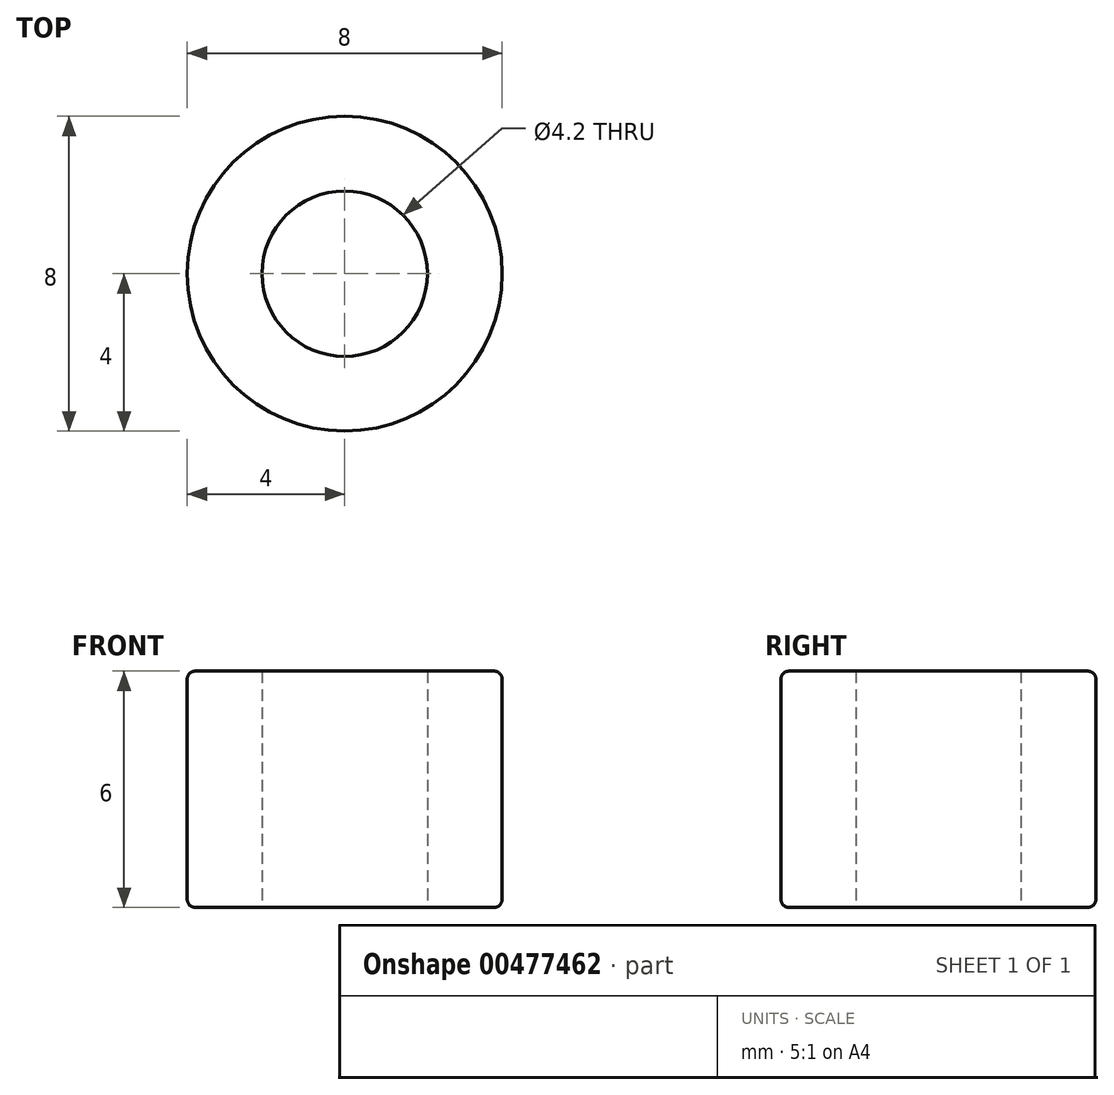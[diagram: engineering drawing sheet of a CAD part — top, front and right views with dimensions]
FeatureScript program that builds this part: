
annotation { "Feature Type Name" : "Feature", "Feature Type Description" : "" }
export const myFeature = defineFeature(function(context is Context, id is Id, definition is map)
    precondition{}
    {
        {
            var Q0;
            Q0=qCreatedBy(makeId("Front.planeOp"),FACE);
            var sketch = newSketch(context, id + "F0", { "sketchPlane" : qUnion([Q0])});
            skLineSegment(sketch, "E0.bottom", {"start": v(-2.1, 0) * mm, "end": v(-3.8, 0) * mm});
            skLineSegment(sketch, "E0.top", {"start": v(-2.1, 6) * mm, "end": v(-3.8, 6) * mm});
            skLineSegment(sketch, "E0.left", {"start": v(-2.1, 0) * mm, "end": v(-2.1, 6) * mm});
            skLineSegment(sketch, "E0.right", {"start": v(-4, 0.2) * mm, "end": v(-4, 5.8) * mm});
            skLineSegment(sketch, "E1", {"start": v(0, 0) * mm, "end": v(0, 8.3) * mm, "construction": true});
            skLineSegment(sketch, "E2.MirrorCS", {"start": v(4, 0) * mm, "end": v(4, 6) * mm, "construction": true});
            skLineSegment(sketch, "E3.MirrorCS", {"start": v(2.1, 0) * mm, "end": v(4, 0) * mm, "construction": true});
            skLineSegment(sketch, "E4.MirrorCS", {"start": v(2.1, 6) * mm, "end": v(4, 6) * mm, "construction": true});
            skLineSegment(sketch, "E5.MirrorCS", {"start": v(2.1, 0) * mm, "end": v(2.1, 6) * mm, "construction": true});
            skPoint(sketch, "E6.visualSharp", {"position": v(-4, 6) * mm});
            skArc(sketch, "E6.filletArc", {"start": v(-3.8, 6) * mm, "mid": v(-3.94, 5.94) * mm, "end": v(-4, 5.8) * mm});
            skPoint(sketch, "E7.visualSharp", {"position": v(-4, 0) * mm});
            skArc(sketch, "E7.filletArc", {"start": v(-4, 0.2) * mm, "mid": v(-3.94, 0.06) * mm, "end": v(-3.8, 0) * mm});
            skSolve(sketch);
        }
        {
            var Q0;
            Q0=makeQuery(id+"F0.imprint","IMPRINT",FACE,{"disambiguationData":[TD([[makeQuery(id+"F0.imprint","IMPRINT",EDGE,{"derivedFrom":sQuery(id+"F0.wireOp",EDGE,"E0.bottom")}),-1.0]])]});
            var Q1;
            Q1=sQuery(id+"F0.wireOp",EDGE,"E1");
            revolve(context, id + "F1", {"entities" : qUnion([Q0]), "axis" : qUnion([Q1]), "revolveType" : RevolveType.FULL});
        }
    });
